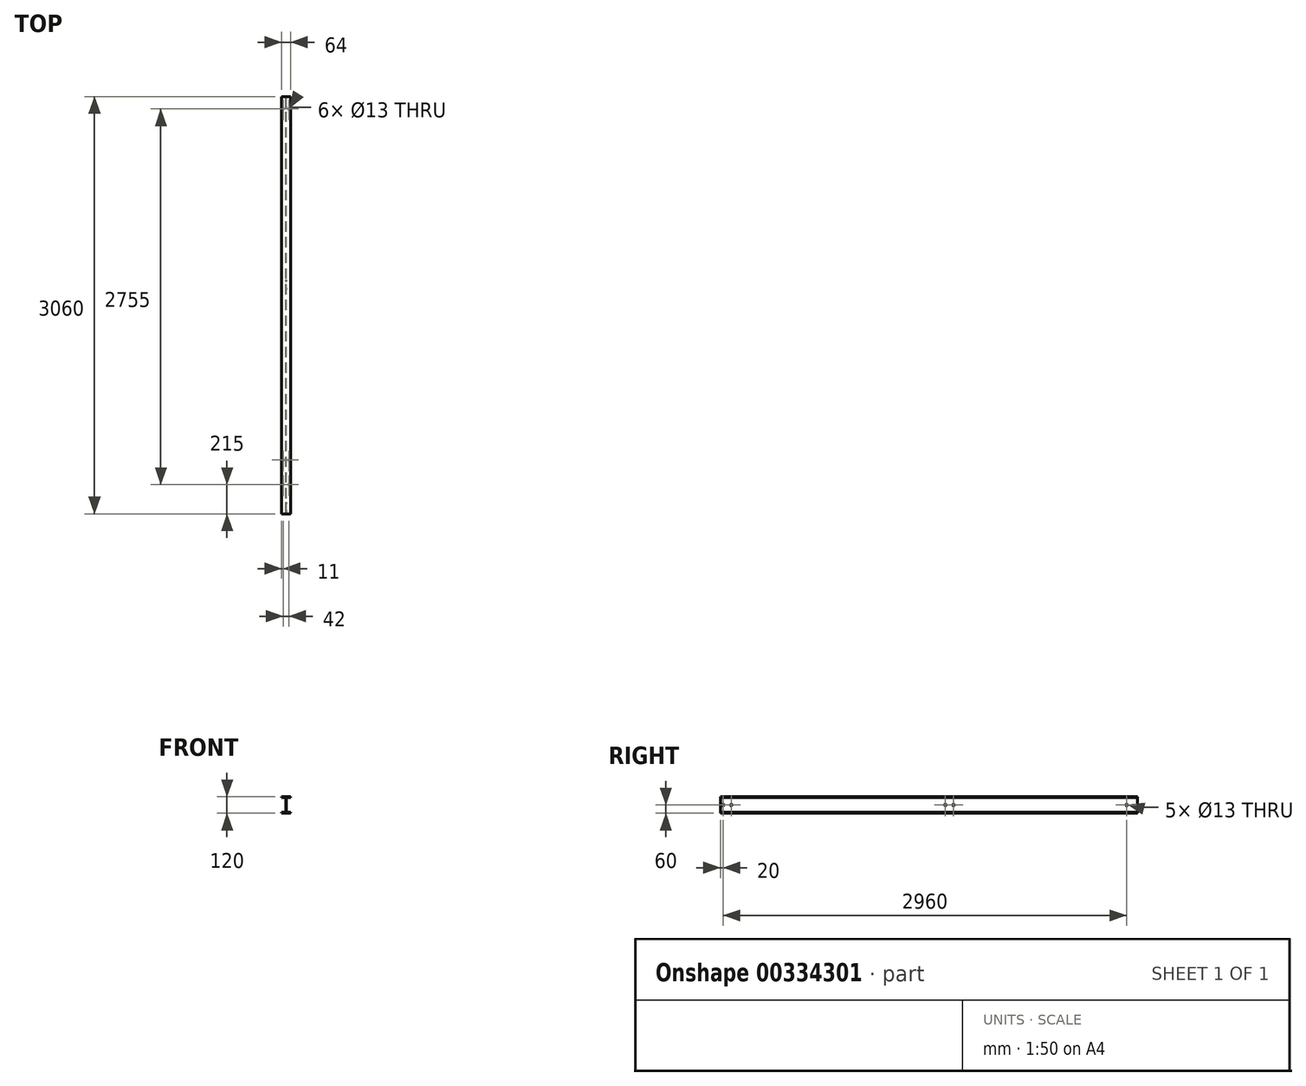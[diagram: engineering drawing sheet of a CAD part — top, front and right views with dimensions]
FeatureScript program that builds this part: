
annotation { "Feature Type Name" : "Feature", "Feature Type Description" : "" }
export const myFeature = defineFeature(function(context is Context, id is Id, definition is map)
    precondition{}
    {
        {
            var Q0;
            Q0=qCreatedBy(makeId("Front.planeOp"),FACE);
            var sketch = newSketch(context, id + "F0", { "sketchPlane" : qUnion([Q0])});
            skLineSegment(sketch, "E0", {"start": v(-32, 0) * mm, "end": v(32, 0) * mm});
            skLineSegment(sketch, "E1", {"start": v(32, 0) * mm, "end": v(32, 6.3) * mm});
            skLineSegment(sketch, "E2", {"start": v(32, 6.3) * mm, "end": v(9.2, 6.3) * mm});
            skLineSegment(sketch, "E3", {"start": v(2.2, 13.3) * mm, "end": v(2.2, 106.7) * mm});
            skLineSegment(sketch, "E4", {"start": v(9.2, 113.7) * mm, "end": v(32, 113.7) * mm});
            skLineSegment(sketch, "E5", {"start": v(32, 113.7) * mm, "end": v(32, 120) * mm});
            skLineSegment(sketch, "E6", {"start": v(32, 120) * mm, "end": v(-32, 120) * mm});
            skLineSegment(sketch, "E7", {"start": v(-32, 120) * mm, "end": v(-32, 113.7) * mm});
            skLineSegment(sketch, "E8", {"start": v(-32, 113.7) * mm, "end": v(-9.2, 113.7) * mm});
            skLineSegment(sketch, "E9", {"start": v(-2.2, 106.7) * mm, "end": v(-2.2, 13.3) * mm});
            skLineSegment(sketch, "E10", {"start": v(-9.2, 6.3) * mm, "end": v(-32, 6.3) * mm});
            skLineSegment(sketch, "E11", {"start": v(-32, 6.3) * mm, "end": v(-32, 0) * mm});
            skLineSegment(sketch, "E12", {"start": v(0, 0) * mm, "end": v(0, 0) * mm});
            skPoint(sketch, "E13.visualSharp", {"position": v(-2.2, 113.7) * mm});
            skArc(sketch, "E13.filletArc", {"start": v(-2.2, 106.7) * mm, "mid": v(-4.25, 111.65) * mm, "end": v(-9.2, 113.7) * mm});
            skPoint(sketch, "E14.visualSharp", {"position": v(-2.2, 6.3) * mm});
            skArc(sketch, "E14.filletArc", {"start": v(-9.2, 6.3) * mm, "mid": v(-4.25, 8.35) * mm, "end": v(-2.2, 13.3) * mm});
            skPoint(sketch, "E15.visualSharp", {"position": v(2.2, 6.3) * mm});
            skArc(sketch, "E15.filletArc", {"start": v(2.2, 13.3) * mm, "mid": v(4.25, 8.35) * mm, "end": v(9.2, 6.3) * mm});
            skPoint(sketch, "E16.visualSharp", {"position": v(2.2, 113.7) * mm});
            skArc(sketch, "E16.filletArc", {"start": v(9.2, 113.7) * mm, "mid": v(4.25, 111.65) * mm, "end": v(2.2, 106.7) * mm});
            skSolve(sketch);
        }
        {
            var Q0;
            Q0=makeQuery(id+"F0.imprint","IMPRINT",FACE,{"disambiguationData":[TD([[makeQuery(id+"F0.imprint","IMPRINT",EDGE,{"derivedFrom":sQuery(id+"F0.wireOp",EDGE,"E0")}),1.0]])]});
            extrude(context, id + "F1", {"entities" : qUnion([Q0]), "depth" : 300 * mm, "hasSecondDirection" : true, "secondDirectionOppositeDirection" : true, "secondDirectionDepth" : 2760 * mm});
        }
        {
            var Q0;
            Q0=makeQuery(id+"F1.opExtrude","SWEPT_FACE",FACE,{"disambiguationData":[OSD([sQuery(id+"F0.wireOp",EDGE,"E0")])]});
            var sketch = newSketch(context, id + "F2", { "sketchPlane" : qUnion([Q0])});
            skLineSegment(sketch, "E17.bottom", {"start": v(21, -95) * mm, "end": v(-21, -95) * mm, "construction": true});
            skLineSegment(sketch, "E17.top", {"start": v(21, 85) * mm, "end": v(-21, 85) * mm, "construction": true});
            skLineSegment(sketch, "E17.left", {"start": v(21, -95) * mm, "end": v(21, 85) * mm, "construction": true});
            skLineSegment(sketch, "E17.right", {"start": v(-21, -95) * mm, "end": v(-21, 85) * mm, "construction": true});
            skPoint(sketch, "E17.middle", {"position": v(0, -5) * mm});
            skCircle(sketch, "E18", {"center": v(21, 85) * mm, "radius": 6.5 * mm});
            skCircle(sketch, "E19", {"center": v(21, -95) * mm, "radius": 6.5 * mm});
            skCircle(sketch, "E20", {"center": v(-21, -95) * mm, "radius": 6.5 * mm});
            skCircle(sketch, "E21", {"center": v(-21, 85) * mm, "radius": 6.5 * mm});
            skLineSegment(sketch, "E22.bottom", {"start": v(21, -2850) * mm, "end": v(-21, -2850) * mm, "construction": true});
            skLineSegment(sketch, "E22.top", {"start": v(21, -2670) * mm, "end": v(-21, -2670) * mm, "construction": true});
            skLineSegment(sketch, "E22.left", {"start": v(21, -2850) * mm, "end": v(21, -2670) * mm, "construction": true});
            skLineSegment(sketch, "E22.right", {"start": v(-21, -2850) * mm, "end": v(-21, -2670) * mm, "construction": true});
            skPoint(sketch, "E22.middle", {"position": v(0, -2760) * mm});
            skPoint(sketch, "E22.middle.positionSnap0", {"position": v(0, -95) * mm});
            skPoint(sketch, "E22.centerSnap0", {"position": v(0, -95) * mm});
            skCircle(sketch, "E23", {"center": v(-21, -2670) * mm, "radius": 6.5 * mm});
            skCircle(sketch, "E24", {"center": v(21, -2670) * mm, "radius": 6.5 * mm});
            skCircle(sketch, "E25", {"center": v(-21, -2850) * mm, "radius": 6.5 * mm, "construction": true});
            skCircle(sketch, "E26", {"center": v(21, -2850) * mm, "radius": 6.5 * mm, "construction": true});
            skSolve(sketch);
        }
        {
            var Q0;
            Q0=makeQuery(id+"F2.imprint","IMPRINT",FACE,{"disambiguationData":[TD([[makeQuery(id+"F2.imprint","IMPRINT",EDGE,{"derivedFrom":sQuery(id+"F2.wireOp",EDGE,"JJcsFfbY-181H-b44I-lAzz-ahYGcjGX36jE")}),1.0]])]});
            var Q1;
            Q1=makeQuery(id+"F2.imprint","IMPRINT",FACE,{"disambiguationData":[TD([[makeQuery(id+"F2.imprint","IMPRINT",EDGE,{"derivedFrom":sQuery(id+"F2.wireOp",EDGE,"8X0YDoZR-MKSx-xxUy-kiRu-iMODx4XVsFsO")}),1.0]])]});
            var Q2;
            Q2=makeQuery(id+"F2.imprint","IMPRINT",FACE,{"disambiguationData":[TD([[makeQuery(id+"F2.imprint","IMPRINT",EDGE,{"derivedFrom":sQuery(id+"F2.wireOp",EDGE,"7u1V7NTp-PA7n-3RXo-sr4M-a3gBre18wiXg")}),1.0]])]});
            var Q3;
            Q3=makeQuery(id+"F2.imprint","IMPRINT",FACE,{"disambiguationData":[TD([[makeQuery(id+"F2.imprint","IMPRINT",EDGE,{"derivedFrom":sQuery(id+"F2.wireOp",EDGE,"P3kTRWrh-zypR-1Pc7-TaIP-jTxsZJOuPHQd")}),1.0]])]});
            var Q4;
            Q4=makeQuery(id+"F2.imprint","IMPRINT",FACE,{"disambiguationData":[TD([[makeQuery(id+"F2.imprint","IMPRINT",EDGE,{"derivedFrom":sQuery(id+"F2.wireOp",EDGE,"dIOHaGGm-riHm-lTID-DCxn-ymXNWbhd4pZG")}),1.0]])]});
            var Q5;
            Q5=makeQuery(id+"F2.imprint","IMPRINT",FACE,{"disambiguationData":[TD([[makeQuery(id+"F2.imprint","IMPRINT",EDGE,{"derivedFrom":sQuery(id+"F2.wireOp",EDGE,"vp5bpoyW-BOQE-W55p-YgiJ-HtZX2Kjx4qEI")}),1.0]])]});
            var Q6;
            Q6=makeQuery(id+"F2.imprint","IMPRINT",FACE,{"disambiguationData":[TD([[makeQuery(id+"F2.imprint","IMPRINT",EDGE,{"derivedFrom":sQuery(id+"F2.wireOp",EDGE,"yILJJugs-jyyq-eTye-5h8z-FDoijVoQVvbv")}),1.0]])]});
            var Q7;
            Q7=makeQuery(id+"F2.imprint","IMPRINT",FACE,{"disambiguationData":[TD([[makeQuery(id+"F2.imprint","IMPRINT",EDGE,{"derivedFrom":sQuery(id+"F2.wireOp",EDGE,"QoqENZRi-UZpU-HqW0-CNnS-FCZrDTomPy0M")}),1.0]])]});
            var Q8;
            Q8=makeQuery(id+"F2.imprint","IMPRINT",FACE,{"disambiguationData":[TD([[makeQuery(id+"F2.imprint","IMPRINT",EDGE,{"derivedFrom":sQuery(id+"F2.wireOp",EDGE,"E18")}),1.0]])]});
            var Q9;
            Q9=makeQuery(id+"F2.imprint","IMPRINT",FACE,{"disambiguationData":[TD([[makeQuery(id+"F2.imprint","IMPRINT",EDGE,{"derivedFrom":sQuery(id+"F2.wireOp",EDGE,"E21")}),1.0]])]});
            var Q10;
            Q10=makeQuery(id+"F2.imprint","IMPRINT",FACE,{"disambiguationData":[TD([[makeQuery(id+"F2.imprint","IMPRINT",EDGE,{"derivedFrom":sQuery(id+"F2.wireOp",EDGE,"E20")}),1.0]])]});
            var Q11;
            Q11=makeQuery(id+"F2.imprint","IMPRINT",FACE,{"disambiguationData":[TD([[makeQuery(id+"F2.imprint","IMPRINT",EDGE,{"derivedFrom":sQuery(id+"F2.wireOp",EDGE,"E19")}),1.0]])]});
            var Q12;
            Q12=makeQuery(id+"F2.imprint","IMPRINT",FACE,{"disambiguationData":[TD([[makeQuery(id+"F2.imprint","IMPRINT",EDGE,{"derivedFrom":sQuery(id+"F2.wireOp",EDGE,"E23")}),1.0]])]});
            var Q13;
            Q13=makeQuery(id+"F2.imprint","IMPRINT",FACE,{"disambiguationData":[TD([[makeQuery(id+"F2.imprint","IMPRINT",EDGE,{"derivedFrom":sQuery(id+"F2.wireOp",EDGE,"E24")}),1.0]])]});
            var Q14;
            Q14=makeQuery(id+"F2.imprint","IMPRINT",FACE,{"disambiguationData":[TD([[makeQuery(id+"F2.imprint","IMPRINT",EDGE,{"derivedFrom":sQuery(id+"F2.wireOp",EDGE,"E26")}),1.0]])]});
            extrude(context, id + "F3", {"entities" : qUnion([Q0, Q1, Q2, Q3, Q4, Q5, Q6, Q7, Q8, Q9, Q10, Q11, Q12, Q13, Q14]), "operationType" : NewBodyOperationType.REMOVE, "endBound" : BoundingType.UP_TO_NEXT, "oppositeDirection" : true, "depth" : 25 * mm});
        }
        {
            var Q0;
            Q0=makeQuery(id+"F1.opExtrude","SWEPT_FACE",FACE,{"disambiguationData":[OSD([sQuery(id+"F0.wireOp",EDGE,"E3")])]});
            var sketch = newSketch(context, id + "F4", { "sketchPlane" : qUnion([Q0])});
            skLineSegment(sketch, "E27", {"start": v(2760, 60) * mm, "end": v(2680, 60) * mm, "construction": true});
            skPoint(sketch, "E27.endSnap0", {"position": v(2760, 60) * mm});
            skCircle(sketch, "E28", {"center": v(2680, 60) * mm, "radius": 6.5 * mm});
            skCircle(sketch, "E29", {"center": v(-280, 60) * mm, "radius": 6.5 * mm});
            skPoint(sketch, "E29.centerSnap0", {"position": v(-300, 60) * mm});
            skCircle(sketch, "E30", {"center": v(-220, 60) * mm, "radius": 6.5 * mm});
            skCircle(sketch, "E31", {"center": v(1350, 60) * mm, "radius": 6.5 * mm});
            skCircle(sketch, "E32", {"center": v(1410, 60) * mm, "radius": 6.5 * mm});
            skSolve(sketch);
        }
        {
            var Q0;
            Q0=qSketchRegion(id+"F4",true);
            extrude(context, id + "F5", {"entities" : qUnion([Q0]), "operationType" : NewBodyOperationType.REMOVE, "endBound" : BoundingType.THROUGH_ALL, "oppositeDirection" : true, "depth" : 25 * mm});
        }
    });
